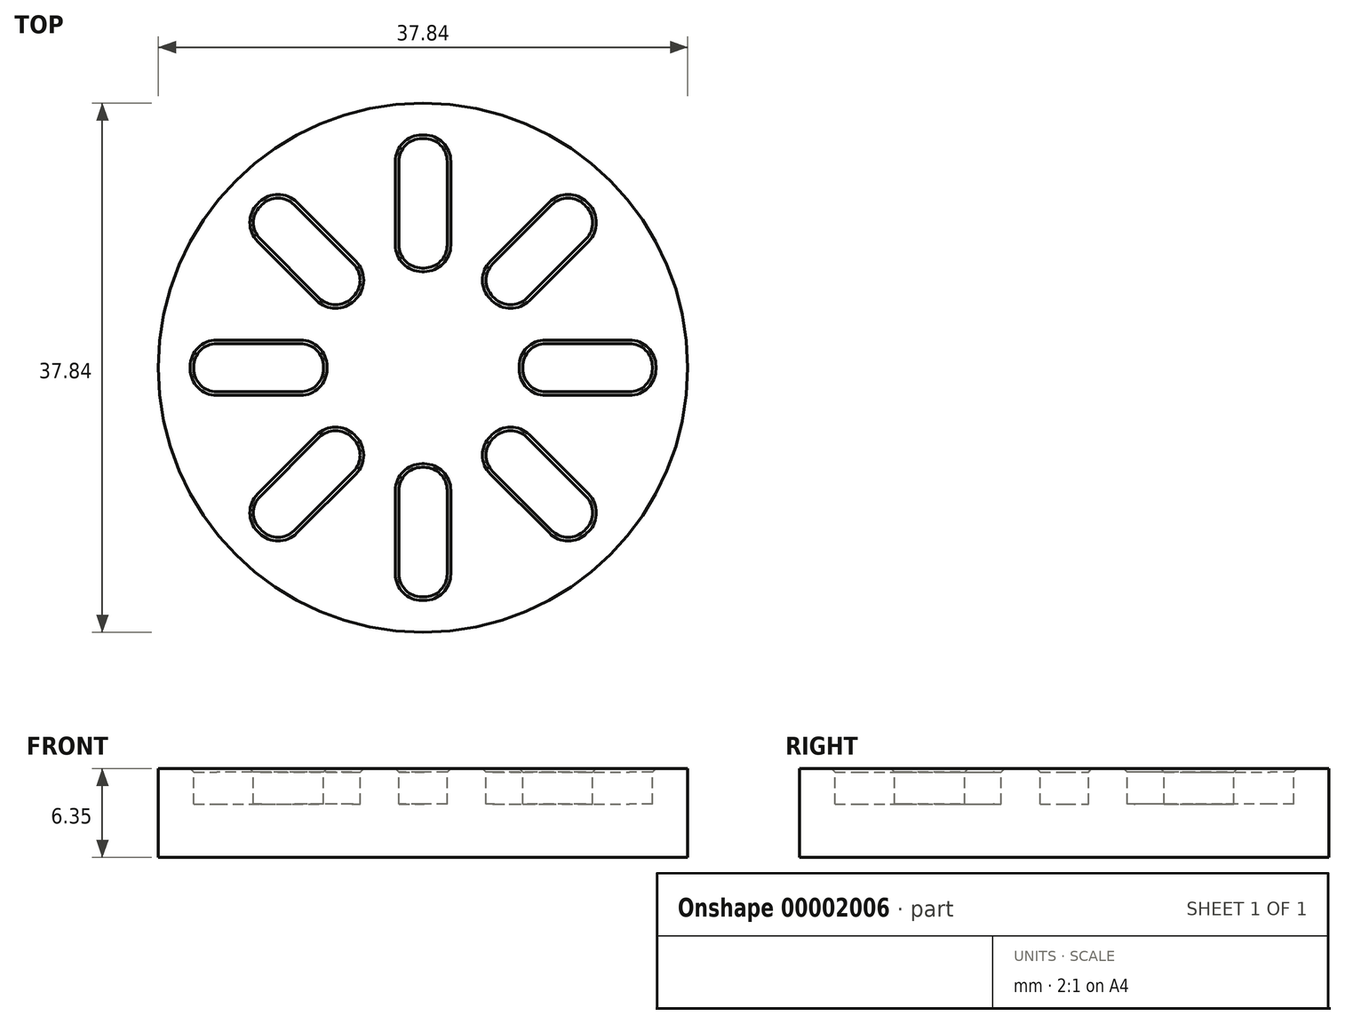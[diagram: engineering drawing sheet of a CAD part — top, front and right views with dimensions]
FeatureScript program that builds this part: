
annotation { "Feature Type Name" : "Feature", "Feature Type Description" : "" }
export const myFeature = defineFeature(function(context is Context, id is Id, definition is map)
    precondition{}
    {
        {
            var Q0;
            Q0=qCreatedBy(makeId("Top.planeOp"),FACE);
            var sketch = newSketch(context, id + "F0", { "sketchPlane" : qUnion([Q0])});
            skCircle(sketch, "E0", {"center": v(0, 0) * mm, "radius": 18.92 * mm});
            skCircle(sketch, "E1", {"center": v(0, 0) * mm, "radius": 4.58 * mm});
            skLineSegment(sketch, "E2", {"start": v(0, 7.12) * mm, "end": v(0, 16.4) * mm});
            skLineSegment(sketch, "E3", {"start": v(0, 16.4) * mm, "end": v(-0.08, 16.4) * mm});
            skLineSegment(sketch, "E4", {"start": v(-0.08, 7.12) * mm, "end": v(0, 7.12) * mm});
            skLineSegment(sketch, "E5", {"start": v(0.08, 16.4) * mm, "end": v(0, 16.4) * mm});
            skLineSegment(sketch, "E6", {"start": v(0, 7.12) * mm, "end": v(0.08, 7.12) * mm});
            skPoint(sketch, "E7.visualSharp", {"position": v(-1.73, 16.4) * mm});
            skArc(sketch, "E7.filletArc", {"start": v(-0.08, 16.4) * mm, "mid": v(-1.24, 15.91) * mm, "end": v(-1.73, 14.74) * mm});
            skPoint(sketch, "E8.visualSharp", {"position": v(1.73, 16.4) * mm});
            skArc(sketch, "E8.filletArc", {"start": v(1.73, 14.74) * mm, "mid": v(1.24, 15.91) * mm, "end": v(0.08, 16.4) * mm});
            skPoint(sketch, "E9.visualSharp", {"position": v(1.73, 7.12) * mm});
            skPoint(sketch, "E10.visualSharp", {"position": v(-1.73, 7.12) * mm});
            skLineSegment(sketch, "E11", {"start": v(-16.4, 0) * mm, "end": v(-16.4, 0.08) * mm});
            skLineSegment(sketch, "E12", {"start": v(-14.74, 1.73) * mm, "end": v(-8.78, 1.73) * mm});
            skLineSegment(sketch, "E13", {"start": v(-7.12, 0.08) * mm, "end": v(-7.12, 0) * mm});
            skLineSegment(sketch, "E14", {"start": v(-8.78, -1.73) * mm, "end": v(-14.74, -1.73) * mm});
            skLineSegment(sketch, "E15", {"start": v(-16.4, -0.08) * mm, "end": v(-16.4, 0) * mm});
            skLineSegment(sketch, "E16", {"start": v(-7.12, -0.08) * mm, "end": v(-7.12, 0) * mm});
            skPoint(sketch, "E17.visualSharp", {"position": v(-16.4, 1.73) * mm});
            skArc(sketch, "E17.filletArc", {"start": v(-14.74, 1.73) * mm, "mid": v(-15.91, 1.24) * mm, "end": v(-16.4, 0.08) * mm});
            skPoint(sketch, "E18.visualSharp", {"position": v(-16.4, -1.73) * mm});
            skArc(sketch, "E18.filletArc", {"start": v(-16.4, -0.08) * mm, "mid": v(-15.91, -1.24) * mm, "end": v(-14.74, -1.73) * mm});
            skPoint(sketch, "E19.visualSharp", {"position": v(-7.12, -1.73) * mm});
            skArc(sketch, "E19.filletArc", {"start": v(-8.78, -1.73) * mm, "mid": v(-7.6, -1.24) * mm, "end": v(-7.12, -0.08) * mm});
            skPoint(sketch, "E20.visualSharp", {"position": v(-7.12, 1.73) * mm});
            skArc(sketch, "E20.filletArc", {"start": v(-7.12, 0.08) * mm, "mid": v(-7.6, 1.24) * mm, "end": v(-8.78, 1.73) * mm});
            skLineSegment(sketch, "E21", {"start": v(7.12, 0) * mm, "end": v(16.4, 0) * mm});
            skLineSegment(sketch, "E22", {"start": v(16.4, 0) * mm, "end": v(16.4, 0.08) * mm});
            skLineSegment(sketch, "E23", {"start": v(14.74, 1.73) * mm, "end": v(8.78, 1.73) * mm});
            skLineSegment(sketch, "E24", {"start": v(7.12, 0.08) * mm, "end": v(7.12, 0) * mm});
            skLineSegment(sketch, "E25", {"start": v(7.12, 0) * mm, "end": v(7.12, -0.08) * mm});
            skLineSegment(sketch, "E26", {"start": v(8.78, -1.73) * mm, "end": v(14.74, -1.73) * mm});
            skLineSegment(sketch, "E27", {"start": v(16.4, -0.08) * mm, "end": v(16.4, 0) * mm});
            skPoint(sketch, "E28.visualSharp", {"position": v(7.12, 1.73) * mm});
            skArc(sketch, "E28.filletArc", {"start": v(8.78, 1.73) * mm, "mid": v(7.6, 1.24) * mm, "end": v(7.12, 0.08) * mm});
            skPoint(sketch, "E29.visualSharp", {"position": v(16.4, 1.73) * mm});
            skArc(sketch, "E29.filletArc", {"start": v(16.4, 0.08) * mm, "mid": v(15.91, 1.24) * mm, "end": v(14.74, 1.73) * mm});
            skPoint(sketch, "E30.visualSharp", {"position": v(16.4, -1.73) * mm});
            skArc(sketch, "E30.filletArc", {"start": v(14.74, -1.73) * mm, "mid": v(15.91, -1.24) * mm, "end": v(16.4, -0.08) * mm});
            skPoint(sketch, "E31.visualSharp", {"position": v(7.12, -1.73) * mm});
            skArc(sketch, "E31.filletArc", {"start": v(7.12, -0.08) * mm, "mid": v(7.6, -1.24) * mm, "end": v(8.78, -1.73) * mm});
            skLineSegment(sketch, "E32", {"start": v(-0.08, 7.12) * mm, "end": v(-0.08, 7.12) * mm});
            skLineSegment(sketch, "E33", {"start": v(0.08, 7.12) * mm, "end": v(0.08, 7.12) * mm});
            skLineSegment(sketch, "E34", {"start": v(-1.73, 14.74) * mm, "end": v(-1.73, 8.78) * mm});
            skLineSegment(sketch, "E35", {"start": v(1.73, 14.74) * mm, "end": v(1.73, 8.78) * mm});
            skArc(sketch, "E36.filletArc", {"start": v(-1.73, 8.78) * mm, "mid": v(-1.24, 7.6) * mm, "end": v(-0.08, 7.12) * mm});
            skArc(sketch, "E37.filletArc", {"start": v(0.08, 7.12) * mm, "mid": v(1.24, 7.6) * mm, "end": v(1.73, 8.78) * mm});
            skLineSegment(sketch, "E38", {"start": v(0, -7.12) * mm, "end": v(0, -16.4) * mm});
            skLineSegment(sketch, "E39", {"start": v(0, -16.4) * mm, "end": v(0.08, -16.4) * mm});
            skLineSegment(sketch, "E40", {"start": v(1.73, -14.74) * mm, "end": v(1.73, -8.78) * mm});
            skLineSegment(sketch, "E41", {"start": v(0.08, -7.12) * mm, "end": v(0, -7.12) * mm});
            skLineSegment(sketch, "E42", {"start": v(0, -7.12) * mm, "end": v(-0.08, -7.12) * mm});
            skLineSegment(sketch, "E43", {"start": v(-1.73, -8.78) * mm, "end": v(-1.73, -14.74) * mm});
            skLineSegment(sketch, "E44", {"start": v(-0.08, -16.4) * mm, "end": v(0, -16.4) * mm});
            skPoint(sketch, "E45.visualSharp", {"position": v(-1.73, -7.12) * mm});
            skArc(sketch, "E45.filletArc", {"start": v(-0.08, -7.12) * mm, "mid": v(-1.24, -7.6) * mm, "end": v(-1.73, -8.78) * mm});
            skPoint(sketch, "E46.visualSharp", {"position": v(1.73, -7.12) * mm});
            skArc(sketch, "E46.filletArc", {"start": v(1.73, -8.78) * mm, "mid": v(1.24, -7.6) * mm, "end": v(0.08, -7.12) * mm});
            skPoint(sketch, "E47.visualSharp", {"position": v(1.73, -16.4) * mm});
            skArc(sketch, "E47.filletArc", {"start": v(0.08, -16.4) * mm, "mid": v(1.24, -15.91) * mm, "end": v(1.73, -14.74) * mm});
            skPoint(sketch, "E48.visualSharp", {"position": v(-1.73, -16.4) * mm});
            skArc(sketch, "E48.filletArc", {"start": v(-1.73, -14.74) * mm, "mid": v(-1.24, -15.91) * mm, "end": v(-0.08, -16.4) * mm});
            skLineSegment(sketch, "E49", {"start": v(5.04, 5.04) * mm, "end": v(11.6, 11.6) * mm});
            skLineSegment(sketch, "E50", {"start": v(5.04, 5.04) * mm, "end": v(4.98, 5.1) * mm});
            skLineSegment(sketch, "E51", {"start": v(4.98, 7.43) * mm, "end": v(9.2, 11.65) * mm});
            skLineSegment(sketch, "E52", {"start": v(11.54, 11.65) * mm, "end": v(11.6, 11.6) * mm});
            skLineSegment(sketch, "E53", {"start": v(11.6, 11.6) * mm, "end": v(11.65, 11.54) * mm});
            skLineSegment(sketch, "E54", {"start": v(11.65, 9.2) * mm, "end": v(7.43, 4.98) * mm});
            skLineSegment(sketch, "E55", {"start": v(5.1, 4.98) * mm, "end": v(5.04, 5.04) * mm});
            skPoint(sketch, "E56.visualSharp", {"position": v(10.37, 12.81) * mm});
            skArc(sketch, "E56.filletArc", {"start": v(11.54, 11.65) * mm, "mid": v(10.37, 12.13) * mm, "end": v(9.2, 11.65) * mm});
            skPoint(sketch, "E57.visualSharp", {"position": v(12.81, 10.37) * mm});
            skArc(sketch, "E57.filletArc", {"start": v(11.65, 9.2) * mm, "mid": v(12.13, 10.37) * mm, "end": v(11.65, 11.54) * mm});
            skPoint(sketch, "E58.visualSharp", {"position": v(6.26, 3.82) * mm});
            skArc(sketch, "E58.filletArc", {"start": v(5.1, 4.98) * mm, "mid": v(6.26, 4.5) * mm, "end": v(7.43, 4.98) * mm});
            skPoint(sketch, "E59.visualSharp", {"position": v(3.82, 6.26) * mm});
            skArc(sketch, "E59.filletArc", {"start": v(4.98, 7.43) * mm, "mid": v(4.5, 6.26) * mm, "end": v(4.98, 5.1) * mm});
            skLineSegment(sketch, "E60", {"start": v(-5.04, 5.04) * mm, "end": v(-11.6, 11.6) * mm});
            skLineSegment(sketch, "E61", {"start": v(-5.04, 5.04) * mm, "end": v(-4.98, 5.1) * mm});
            skLineSegment(sketch, "E62", {"start": v(-4.98, 7.43) * mm, "end": v(-9.2, 11.65) * mm});
            skLineSegment(sketch, "E63", {"start": v(-11.54, 11.65) * mm, "end": v(-11.6, 11.6) * mm});
            skLineSegment(sketch, "E64", {"start": v(-11.6, 11.6) * mm, "end": v(-11.65, 11.54) * mm});
            skLineSegment(sketch, "E65", {"start": v(-11.65, 9.2) * mm, "end": v(-7.43, 4.98) * mm});
            skLineSegment(sketch, "E66", {"start": v(-5.1, 4.98) * mm, "end": v(-5.04, 5.04) * mm});
            skPoint(sketch, "E67.visualSharp", {"position": v(-10.37, 12.81) * mm});
            skArc(sketch, "E67.filletArc", {"start": v(-9.2, 11.65) * mm, "mid": v(-10.37, 12.13) * mm, "end": v(-11.54, 11.65) * mm});
            skPoint(sketch, "E68.visualSharp", {"position": v(-12.81, 10.37) * mm});
            skArc(sketch, "E68.filletArc", {"start": v(-11.65, 11.54) * mm, "mid": v(-12.13, 10.37) * mm, "end": v(-11.65, 9.2) * mm});
            skPoint(sketch, "E69.visualSharp", {"position": v(-3.82, 6.26) * mm});
            skArc(sketch, "E69.filletArc", {"start": v(-4.98, 5.1) * mm, "mid": v(-4.5, 6.26) * mm, "end": v(-4.98, 7.43) * mm});
            skPoint(sketch, "E70.visualSharp", {"position": v(-6.26, 3.82) * mm});
            skArc(sketch, "E70.filletArc", {"start": v(-7.43, 4.98) * mm, "mid": v(-6.26, 4.5) * mm, "end": v(-5.1, 4.98) * mm});
            skLineSegment(sketch, "E71", {"start": v(-5.04, -5.04) * mm, "end": v(-11.6, -11.6) * mm});
            skLineSegment(sketch, "E72", {"start": v(-5.04, -5.04) * mm, "end": v(-4.98, -5.1) * mm});
            skLineSegment(sketch, "E73", {"start": v(-4.98, -7.43) * mm, "end": v(-9.2, -11.65) * mm});
            skLineSegment(sketch, "E74", {"start": v(-11.54, -11.65) * mm, "end": v(-11.6, -11.6) * mm});
            skLineSegment(sketch, "E75", {"start": v(-11.6, -11.6) * mm, "end": v(-11.65, -11.54) * mm});
            skLineSegment(sketch, "E76", {"start": v(-11.65, -9.2) * mm, "end": v(-7.43, -4.98) * mm});
            skLineSegment(sketch, "E77", {"start": v(-5.1, -4.98) * mm, "end": v(-5.04, -5.04) * mm});
            skLineSegment(sketch, "E78", {"start": v(5.04, -5.04) * mm, "end": v(11.6, -11.6) * mm});
            skLineSegment(sketch, "E79", {"start": v(11.6, -11.6) * mm, "end": v(11.65, -11.54) * mm});
            skLineSegment(sketch, "E80", {"start": v(11.65, -9.2) * mm, "end": v(7.43, -4.98) * mm});
            skLineSegment(sketch, "E81", {"start": v(5.1, -4.98) * mm, "end": v(5.04, -5.04) * mm});
            skLineSegment(sketch, "E82", {"start": v(5.04, -5.04) * mm, "end": v(4.98, -5.1) * mm});
            skLineSegment(sketch, "E83", {"start": v(4.98, -7.43) * mm, "end": v(9.2, -11.65) * mm});
            skLineSegment(sketch, "E84", {"start": v(11.54, -11.65) * mm, "end": v(11.6, -11.6) * mm});
            skPoint(sketch, "E85.visualSharp", {"position": v(-6.26, -3.82) * mm});
            skArc(sketch, "E85.filletArc", {"start": v(-5.1, -4.98) * mm, "mid": v(-6.26, -4.5) * mm, "end": v(-7.43, -4.98) * mm});
            skPoint(sketch, "E86.visualSharp", {"position": v(-3.82, -6.26) * mm});
            skArc(sketch, "E86.filletArc", {"start": v(-4.98, -7.43) * mm, "mid": v(-4.5, -6.26) * mm, "end": v(-4.98, -5.1) * mm});
            skPoint(sketch, "E87.visualSharp", {"position": v(-10.37, -12.81) * mm});
            skArc(sketch, "E87.filletArc", {"start": v(-11.54, -11.65) * mm, "mid": v(-10.37, -12.13) * mm, "end": v(-9.2, -11.65) * mm});
            skPoint(sketch, "E88.visualSharp", {"position": v(-12.81, -10.37) * mm});
            skArc(sketch, "E88.filletArc", {"start": v(-11.65, -9.2) * mm, "mid": v(-12.13, -10.37) * mm, "end": v(-11.65, -11.54) * mm});
            skPoint(sketch, "E89.visualSharp", {"position": v(3.82, -6.26) * mm});
            skArc(sketch, "E89.filletArc", {"start": v(4.98, -5.1) * mm, "mid": v(4.5, -6.26) * mm, "end": v(4.98, -7.43) * mm});
            skPoint(sketch, "E90.visualSharp", {"position": v(12.81, -10.37) * mm});
            skArc(sketch, "E90.filletArc", {"start": v(11.65, -11.54) * mm, "mid": v(12.13, -10.37) * mm, "end": v(11.65, -9.2) * mm});
            skPoint(sketch, "E91.visualSharp", {"position": v(10.37, -12.81) * mm});
            skArc(sketch, "E91.filletArc", {"start": v(9.2, -11.65) * mm, "mid": v(10.37, -12.13) * mm, "end": v(11.54, -11.65) * mm});
            skPoint(sketch, "E92.visualSharp", {"position": v(6.26, -3.82) * mm});
            skArc(sketch, "E92.filletArc", {"start": v(7.43, -4.98) * mm, "mid": v(6.26, -4.5) * mm, "end": v(5.1, -4.98) * mm});
            skSolve(sketch);
        }
        {
            var Q0;
            Q0=makeQuery(id+"F0.imprint","IMPRINT",FACE,{"disambiguationData":[TD([[makeQuery(id+"F0.imprint","IMPRINT",EDGE,{"derivedFrom":sQuery(id+"F0.wireOp",EDGE,"E0")}),1.0]])]});
            extrude(context, id + "F1", {"entities" : qUnion([Q0]), "oppositeDirection" : true, "depth" : 2.54 * mm});
        }
        {
            var Q0;
            Q0=makeQuery(id+"F1.opExtrude","CAP_FACE",FACE,{"disambiguationData":[OSD([sQuery(id+"F0.wireOp",EDGE,"E0"),sQuery(id+"F0.wireOp",EDGE,"E1"),sQuery(id+"F0.wireOp",EDGE,"E3"),sQuery(id+"F0.wireOp",EDGE,"E4"),sQuery(id+"F0.wireOp",EDGE,"E5"),sQuery(id+"F0.wireOp",EDGE,"E6"),sQuery(id+"F0.wireOp",EDGE,"E7.filletArc"),sQuery(id+"F0.wireOp",EDGE,"E8.filletArc"),sQuery(id+"F0.wireOp",EDGE,"E11"),sQuery(id+"F0.wireOp",EDGE,"E12"),sQuery(id+"F0.wireOp",EDGE,"E13"),sQuery(id+"F0.wireOp",EDGE,"E14"),sQuery(id+"F0.wireOp",EDGE,"E15"),sQuery(id+"F0.wireOp",EDGE,"E16"),sQuery(id+"F0.wireOp",EDGE,"E17.filletArc"),sQuery(id+"F0.wireOp",EDGE,"E18.filletArc"),sQuery(id+"F0.wireOp",EDGE,"E19.filletArc"),sQuery(id+"F0.wireOp",EDGE,"E20.filletArc"),sQuery(id+"F0.wireOp",EDGE,"E22"),sQuery(id+"F0.wireOp",EDGE,"E23"),sQuery(id+"F0.wireOp",EDGE,"E24"),sQuery(id+"F0.wireOp",EDGE,"E25"),sQuery(id+"F0.wireOp",EDGE,"E26"),sQuery(id+"F0.wireOp",EDGE,"E27"),sQuery(id+"F0.wireOp",EDGE,"E28.filletArc"),sQuery(id+"F0.wireOp",EDGE,"E29.filletArc"),sQuery(id+"F0.wireOp",EDGE,"E30.filletArc"),sQuery(id+"F0.wireOp",EDGE,"E31.filletArc"),sQuery(id+"F0.wireOp",EDGE,"E34"),sQuery(id+"F0.wireOp",EDGE,"E35"),sQuery(id+"F0.wireOp",EDGE,"E36.filletArc"),sQuery(id+"F0.wireOp",EDGE,"E37.filletArc"),sQuery(id+"F0.wireOp",EDGE,"E39"),sQuery(id+"F0.wireOp",EDGE,"E40"),sQuery(id+"F0.wireOp",EDGE,"E41"),sQuery(id+"F0.wireOp",EDGE,"E42"),sQuery(id+"F0.wireOp",EDGE,"E43"),sQuery(id+"F0.wireOp",EDGE,"E44"),sQuery(id+"F0.wireOp",EDGE,"E45.filletArc"),sQuery(id+"F0.wireOp",EDGE,"E46.filletArc"),sQuery(id+"F0.wireOp",EDGE,"E47.filletArc"),sQuery(id+"F0.wireOp",EDGE,"E48.filletArc"),sQuery(id+"F0.wireOp",EDGE,"E50"),sQuery(id+"F0.wireOp",EDGE,"E51"),sQuery(id+"F0.wireOp",EDGE,"E52"),sQuery(id+"F0.wireOp",EDGE,"E53"),sQuery(id+"F0.wireOp",EDGE,"E54"),sQuery(id+"F0.wireOp",EDGE,"E55"),sQuery(id+"F0.wireOp",EDGE,"E56.filletArc"),sQuery(id+"F0.wireOp",EDGE,"E57.filletArc"),sQuery(id+"F0.wireOp",EDGE,"E58.filletArc"),sQuery(id+"F0.wireOp",EDGE,"E59.filletArc"),sQuery(id+"F0.wireOp",EDGE,"E61"),sQuery(id+"F0.wireOp",EDGE,"E62"),sQuery(id+"F0.wireOp",EDGE,"E63"),sQuery(id+"F0.wireOp",EDGE,"E64"),sQuery(id+"F0.wireOp",EDGE,"E65"),sQuery(id+"F0.wireOp",EDGE,"E66"),sQuery(id+"F0.wireOp",EDGE,"E67.filletArc"),sQuery(id+"F0.wireOp",EDGE,"E68.filletArc"),sQuery(id+"F0.wireOp",EDGE,"E69.filletArc"),sQuery(id+"F0.wireOp",EDGE,"E70.filletArc"),sQuery(id+"F0.wireOp",EDGE,"E72"),sQuery(id+"F0.wireOp",EDGE,"E73"),sQuery(id+"F0.wireOp",EDGE,"E74"),sQuery(id+"F0.wireOp",EDGE,"E75"),sQuery(id+"F0.wireOp",EDGE,"E76"),sQuery(id+"F0.wireOp",EDGE,"E77"),sQuery(id+"F0.wireOp",EDGE,"E79"),sQuery(id+"F0.wireOp",EDGE,"E80"),sQuery(id+"F0.wireOp",EDGE,"E81"),sQuery(id+"F0.wireOp",EDGE,"E82"),sQuery(id+"F0.wireOp",EDGE,"E83"),sQuery(id+"F0.wireOp",EDGE,"E84"),sQuery(id+"F0.wireOp",EDGE,"E85.filletArc"),sQuery(id+"F0.wireOp",EDGE,"E86.filletArc"),sQuery(id+"F0.wireOp",EDGE,"E87.filletArc"),sQuery(id+"F0.wireOp",EDGE,"E88.filletArc"),sQuery(id+"F0.wireOp",EDGE,"E89.filletArc"),sQuery(id+"F0.wireOp",EDGE,"E90.filletArc"),sQuery(id+"F0.wireOp",EDGE,"E91.filletArc"),sQuery(id+"F0.wireOp",EDGE,"E92.filletArc")])],"isStart":false});
            var sketch = newSketch(context, id + "F2", { "sketchPlane" : qUnion([Q0])});
            skCircle(sketch, "E93", {"center": v(0, 0) * mm, "radius": 18.92 * mm});
            skSolve(sketch);
        }
        {
            var Q0;
            {var subQ0=makeQuery(id+"F2.imprint","IMPRINT",EDGE,{"derivedFrom":makeQuery(id+"F1.opExtrude","CAP_EDGE",EDGE,{"disambiguationData":[OSD([sQuery(id+"F0.wireOp",EDGE,"E1")])],"isStart":false})});var subQ6=makeQuery(id+"F2.imprint","IMPRINT",EDGE,{"derivedFrom":makeQuery(id+"F1.opExtrude","CAP_EDGE",EDGE,{"disambiguationData":[OSD([sQuery(id+"F0.wireOp",EDGE,"E7.filletArc")])],"isStart":false})});var subQ15=makeQuery(id+"F2.imprint","IMPRINT",EDGE,{"derivedFrom":makeQuery(id+"F1.opExtrude","CAP_EDGE",EDGE,{"disambiguationData":[OSD([sQuery(id+"F0.wireOp",EDGE,"E12")])],"isStart":false})});var subQ23=makeQuery(id+"F2.imprint","IMPRINT",EDGE,{"derivedFrom":makeQuery(id+"F1.opExtrude","CAP_EDGE",EDGE,{"disambiguationData":[OSD([sQuery(id+"F0.wireOp",EDGE,"E23")])],"isStart":false})});var subQ31=makeQuery(id+"F2.imprint","IMPRINT",EDGE,{"derivedFrom":makeQuery(id+"F1.opExtrude","CAP_EDGE",EDGE,{"disambiguationData":[OSD([sQuery(id+"F0.wireOp",EDGE,"E40")])],"isStart":false})});var subQ39=makeQuery(id+"F2.imprint","IMPRINT",EDGE,{"derivedFrom":makeQuery(id+"F1.opExtrude","CAP_EDGE",EDGE,{"disambiguationData":[OSD([sQuery(id+"F0.wireOp",EDGE,"E51")])],"isStart":false})});var subQ47=makeQuery(id+"F2.imprint","IMPRINT",EDGE,{"derivedFrom":makeQuery(id+"F1.opExtrude","CAP_EDGE",EDGE,{"disambiguationData":[OSD([sQuery(id+"F0.wireOp",EDGE,"E62")])],"isStart":false})});var subQ55=makeQuery(id+"F2.imprint","IMPRINT",EDGE,{"derivedFrom":makeQuery(id+"F1.opExtrude","CAP_EDGE",EDGE,{"disambiguationData":[OSD([sQuery(id+"F0.wireOp",EDGE,"E73")])],"isStart":false})});var subQ62=makeQuery(id+"F2.imprint","IMPRINT",EDGE,{"derivedFrom":makeQuery(id+"F1.opExtrude","CAP_EDGE",EDGE,{"disambiguationData":[OSD([sQuery(id+"F0.wireOp",EDGE,"E80")])],"isStart":false})});Q0=qUnion([makeQuery(id+"F2.imprint","IMPRINT",FACE,{"disambiguationData":[TD([[subQ0,-1.0]])]}),makeQuery(id+"F2.imprint","IMPRINT",FACE,{"disambiguationData":[TD([[subQ6,-1.0]])]}),makeQuery(id+"F2.imprint","IMPRINT",FACE,{"disambiguationData":[TD([[subQ15,1.0]])]}),makeQuery(id+"F2.imprint","IMPRINT",FACE,{"disambiguationData":[TD([[subQ23,-1.0]])]}),makeQuery(id+"F2.imprint","IMPRINT",FACE,{"disambiguationData":[TD([[subQ31,-1.0]])]}),makeQuery(id+"F2.imprint","IMPRINT",FACE,{"disambiguationData":[TD([[subQ39,1.0]])]}),makeQuery(id+"F2.imprint","IMPRINT",FACE,{"disambiguationData":[TD([[subQ47,-1.0]])]}),makeQuery(id+"F2.imprint","IMPRINT",FACE,{"disambiguationData":[TD([[subQ55,1.0]])]}),makeQuery(id+"F2.imprint","IMPRINT",FACE,{"disambiguationData":[TD([[subQ62,-1.0]])]}),makeQuery(id+"F2.imprint","IMPRINT",FACE,{"disambiguationData":[TD([[makeQuery(id+"F2.imprint","IMPRINT",EDGE,{"derivedFrom":sQuery(id+"F2.wireOp",EDGE,"E93")}),-1.0]])]})]);}
            extrude(context, id + "F3", {"entities" : qUnion([Q0]), "operationType" : NewBodyOperationType.ADD, "depth" : 3.8 * mm});
        }
        {
            var Q0;
            Q0=makeQuery(id+"F3.boolean.opBoolean","SPLIT",FACE,{"disambiguationData":[TD([makeQuery(id+"F1.opExtrude","SWEPT_FACE",FACE,{"disambiguationData":[OSD([sQuery(id+"F0.wireOp",EDGE,"E1")])]})])],"derivedFrom":makeQuery(id+"F3.opExtrude","CAP_FACE",FACE,{"disambiguationData":[OSD([sQuery(id+"F2.wireOp",EDGE,"E93")])],"isStart":true})});
            extrude(context, id + "F4", {"entities" : qUnion([Q0]), "operationType" : NewBodyOperationType.ADD, "depth" : 2.54 * mm});
        }
        {
            var Q0;
            Q0=makeQuery(id+"F1.opExtrude","CAP_EDGE",EDGE,{"disambiguationData":[OSD([sQuery(id+"F0.wireOp",EDGE,"E65")])],"isStart":true});
            var Q1;
            Q1=makeQuery(id+"F1.opExtrude","CAP_EDGE",EDGE,{"disambiguationData":[OSD([sQuery(id+"F0.wireOp",EDGE,"E68.filletArc")])],"isStart":true});
            var Q2;
            Q2=makeQuery(id+"F1.opExtrude","CAP_EDGE",EDGE,{"disambiguationData":[OSD([sQuery(id+"F0.wireOp",EDGE,"E67.filletArc")])],"isStart":true});
            var Q3;
            Q3=makeQuery(id+"F1.opExtrude","CAP_EDGE",EDGE,{"disambiguationData":[OSD([sQuery(id+"F0.wireOp",EDGE,"E62")])],"isStart":true});
            var Q4;
            Q4=makeQuery(id+"F1.opExtrude","CAP_EDGE",EDGE,{"disambiguationData":[OSD([sQuery(id+"F0.wireOp",EDGE,"E69.filletArc")])],"isStart":true});
            var Q5;
            Q5=makeQuery(id+"F1.opExtrude","CAP_EDGE",EDGE,{"disambiguationData":[OSD([sQuery(id+"F0.wireOp",EDGE,"E70.filletArc")])],"isStart":true});
            var Q6;
            Q6=makeQuery(id+"F1.opExtrude","CAP_EDGE",EDGE,{"disambiguationData":[OSD([sQuery(id+"F0.wireOp",EDGE,"E63"),sQuery(id+"F0.wireOp",EDGE,"E64")])],"isStart":true});
            var Q7;
            Q7=makeQuery(id+"F1.opExtrude","CAP_EDGE",EDGE,{"disambiguationData":[OSD([sQuery(id+"F0.wireOp",EDGE,"E61"),sQuery(id+"F0.wireOp",EDGE,"E66")])],"isStart":true});
            var Q8;
            Q8=makeQuery(id+"F1.opExtrude","CAP_EDGE",EDGE,{"disambiguationData":[OSD([sQuery(id+"F0.wireOp",EDGE,"E18.filletArc")])],"isStart":true});
            var Q9;
            Q9=makeQuery(id+"F1.opExtrude","CAP_EDGE",EDGE,{"disambiguationData":[OSD([sQuery(id+"F0.wireOp",EDGE,"E11"),sQuery(id+"F0.wireOp",EDGE,"E15")])],"isStart":true});
            var Q10;
            Q10=makeQuery(id+"F1.opExtrude","CAP_EDGE",EDGE,{"disambiguationData":[OSD([sQuery(id+"F0.wireOp",EDGE,"E17.filletArc")])],"isStart":true});
            var Q11;
            Q11=makeQuery(id+"F1.opExtrude","CAP_EDGE",EDGE,{"disambiguationData":[OSD([sQuery(id+"F0.wireOp",EDGE,"E76")])],"isStart":true});
            var Q12;
            Q12=makeQuery(id+"F1.opExtrude","CAP_EDGE",EDGE,{"disambiguationData":[OSD([sQuery(id+"F0.wireOp",EDGE,"E43")])],"isStart":true});
            var Q13;
            Q13=makeQuery(id+"F1.opExtrude","CAP_EDGE",EDGE,{"disambiguationData":[OSD([sQuery(id+"F0.wireOp",EDGE,"E83")])],"isStart":true});
            var Q14;
            Q14=makeQuery(id+"F1.opExtrude","CAP_EDGE",EDGE,{"disambiguationData":[OSD([sQuery(id+"F0.wireOp",EDGE,"E26")])],"isStart":true});
            var Q15;
            Q15=makeQuery(id+"F1.opExtrude","CAP_EDGE",EDGE,{"disambiguationData":[OSD([sQuery(id+"F0.wireOp",EDGE,"E54")])],"isStart":true});
            var Q16;
            Q16=makeQuery(id+"F1.opExtrude","CAP_EDGE",EDGE,{"disambiguationData":[OSD([sQuery(id+"F0.wireOp",EDGE,"E35")])],"isStart":true});
            chamfer(context, id + "F5", {"entities" : qUnion([Q0, Q1, Q2, Q3, Q4, Q5, Q6, Q7, Q8, Q9, Q10, Q11, Q12, Q13, Q14, Q15, Q16]), "width" : 0.25 * mm, "tangentPropagation" : true});
        }
    });
